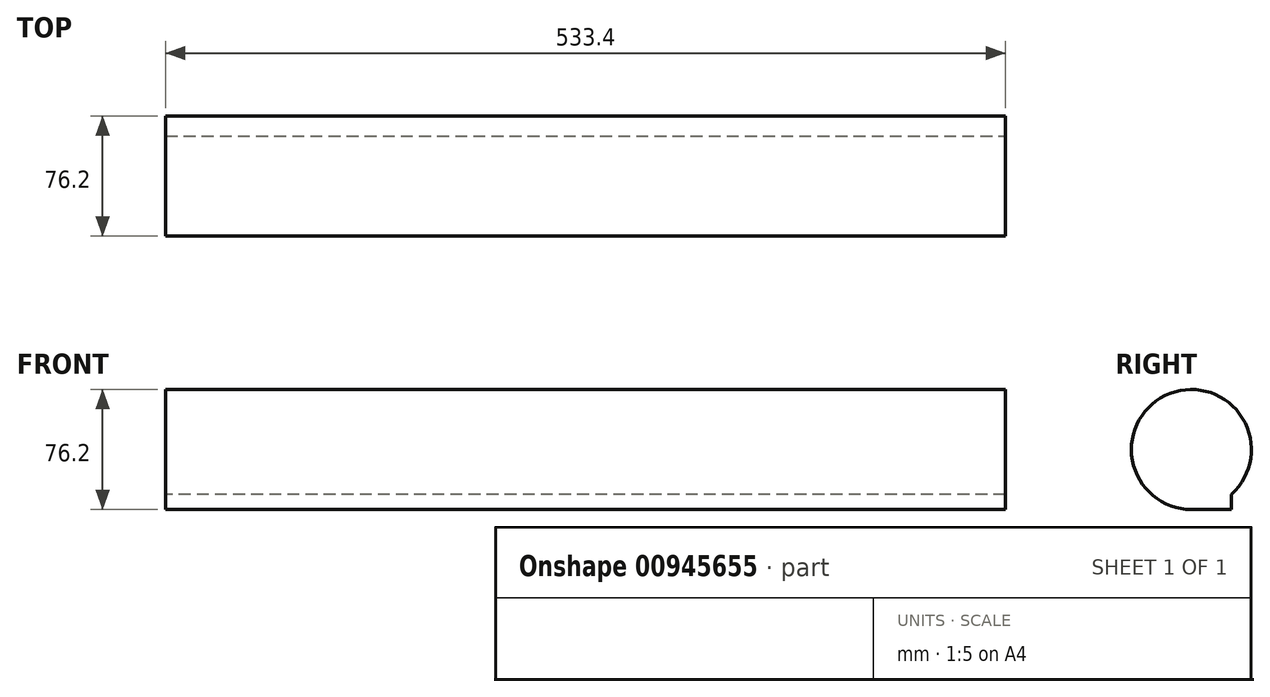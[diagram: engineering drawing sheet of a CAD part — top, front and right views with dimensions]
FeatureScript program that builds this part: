
annotation { "Feature Type Name" : "Feature", "Feature Type Description" : "" }
export const myFeature = defineFeature(function(context is Context, id is Id, definition is map)
    precondition{}
    {
        {
            var Q0;
            Q0=qCreatedBy(makeId("Front.planeOp"),FACE);
            var sketch = newSketch(context, id + "F0", { "sketchPlane" : qUnion([Q0])});
            skLineSegment(sketch, "E0.bottom", {"start": v(-271.23, 38.1) * mm, "end": v(262.17, 38.1) * mm});
            skLineSegment(sketch, "E0.top", {"start": v(-271.23, 0) * mm, "end": v(262.17, 0) * mm});
            skLineSegment(sketch, "E0.left", {"start": v(-271.23, 38.1) * mm, "end": v(-271.23, 0) * mm});
            skLineSegment(sketch, "E0.right", {"start": v(262.17, 38.1) * mm, "end": v(262.17, 0) * mm});
            skSolve(sketch);
        }
        {
            var Q0;
            Q0=qSketchRegion(id+"F0",true);
            extrude(context, id + "F1", {"entities" : qUnion([Q0]), "depth" : 25.4 * mm, "offsetDistance" : 25.4 * mm});
        }
        {
            var Q0;
            Q0=makeQuery(id+"F1.opExtrude","CAP_FACE",FACE,{"disambiguationData":[OSD([sQuery(id+"F0.wireOp",EDGE,"E0.bottom"),sQuery(id+"F0.wireOp",EDGE,"E0.top"),sQuery(id+"F0.wireOp",EDGE,"E0.left"),sQuery(id+"F0.wireOp",EDGE,"E0.right")])],"isStart":false});
            var Q1;
            Q1=makeQuery(id+"F1.opExtrude","CAP_EDGE",EDGE,{"disambiguationData":[OSD([sQuery(id+"F0.wireOp",EDGE,"E0.bottom")])],"isStart":false});
            revolve(context, id + "F2", {"operationType" : NewBodyOperationType.ADD, "surfaceOperationType" : NewSurfaceOperationType.NEW, "entities" : qUnion([Q0]), "axis" : qUnion([Q1]), "revolveType" : RevolveType.FULL});
        }
    });
